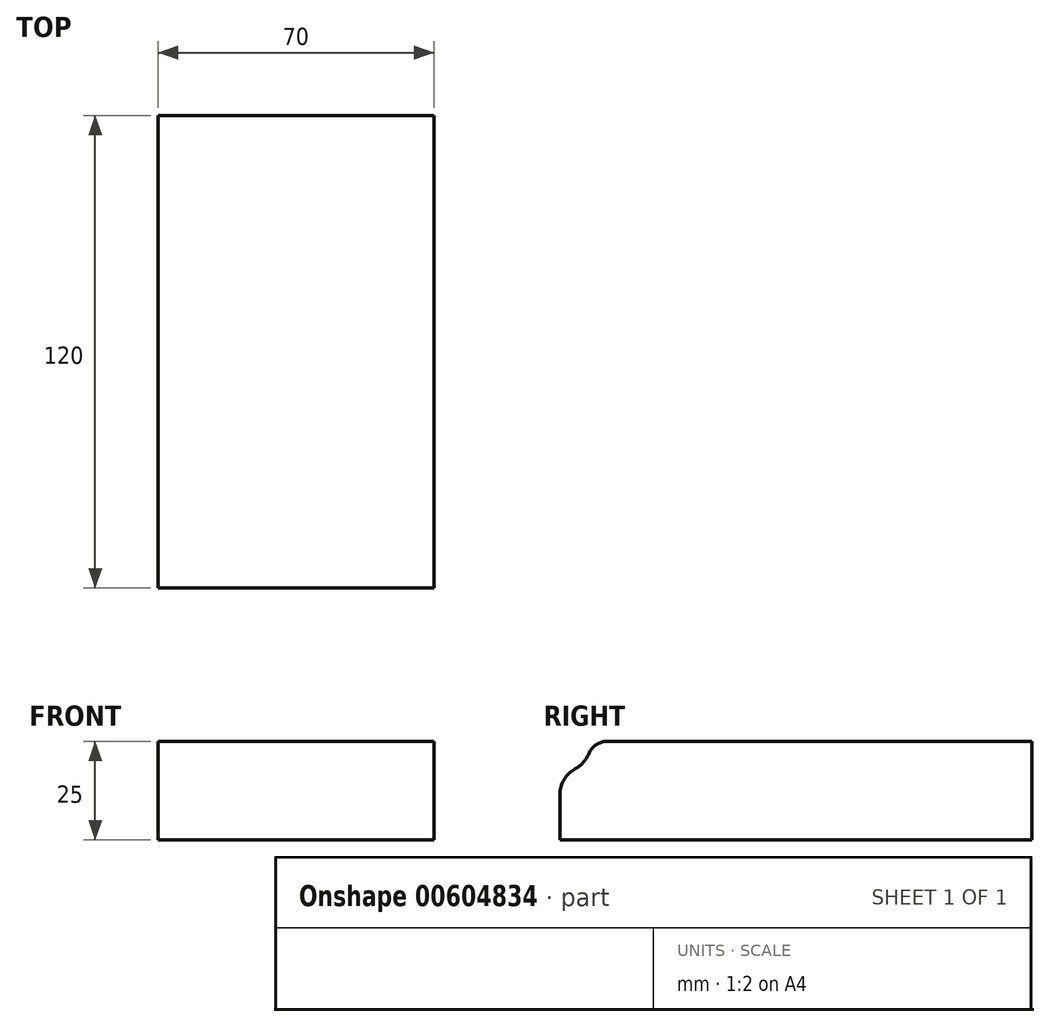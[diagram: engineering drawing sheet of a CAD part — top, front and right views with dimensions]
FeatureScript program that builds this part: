
annotation { "Feature Type Name" : "Feature", "Feature Type Description" : "" }
export const myFeature = defineFeature(function(context is Context, id is Id, definition is map)
    precondition{}
    {
        {
            var Q0;
            Q0=qCreatedBy(makeId("Top.planeOp"),FACE);
            var sketch = newSketch(context, id + "F0", { "sketchPlane" : qUnion([Q0])});
            skLineSegment(sketch, "E0.bottom", {"start": v(-35, -60) * mm, "end": v(35, -60) * mm});
            skLineSegment(sketch, "E0.top", {"start": v(-35, 60) * mm, "end": v(35, 60) * mm});
            skLineSegment(sketch, "E0.left", {"start": v(-35, -60) * mm, "end": v(-35, 60) * mm});
            skLineSegment(sketch, "E0.right", {"start": v(35, -60) * mm, "end": v(35, 60) * mm});
            skPoint(sketch, "E0.middle", {"position": v(0, 0) * mm});
            skSolve(sketch);
        }
        {
            var Q0;
            Q0=makeQuery(id+"F0.imprint","IMPRINT",FACE,{"disambiguationData":[TD([[makeQuery(id+"F0.imprint","IMPRINT",EDGE,{"derivedFrom":sQuery(id+"F0.wireOp",EDGE,"E0.bottom")}),1.0]])]});
            extrude(context, id + "F1", {"entities" : qUnion([Q0]), "depth" : 25 * mm, "offsetDistance" : 25 * mm});
        }
        {
            var Q0;
            Q0=makeQuery(id+"F1.opExtrude","SWEPT_FACE",FACE,{"disambiguationData":[OSD([sQuery(id+"F0.wireOp",EDGE,"E0.right")])]});
            var sketch = newSketch(context, id + "F2", { "sketchPlane" : qUnion([Q0])});
            skCircle(sketch, "E1", {"center": v(-60, 25) * mm, "radius": 8 * mm});
            skSolve(sketch);
        }
        {
            var Q0;
            Q0 = qSketchRegion(id + "F2", true);
            var Q1;
            Q1=makeQuery(id+"F1.opExtrude","SWEPT_FACE",FACE,{"disambiguationData":[OSD([sQuery(id+"F0.wireOp",EDGE,"E0.left")])]});
            extrude(context, id + "F3", {"entities" : qUnion([Q0]), "operationType" : NewBodyOperationType.REMOVE, "endBound" : BoundingType.UP_TO_SURFACE, "oppositeDirection" : true, "depth" : 25 * mm, "endBoundEntityFace" : qUnion([Q1]), "offsetDistance" : 25 * mm});
        }
        {
            var Q0;
            Q0=makeQuery(id+"F3.boolean.opBoolean","INTERSECT",EDGE,{"derivedFrom":[makeQuery(id+"F1.opExtrude","CAP_FACE",FACE,{"disambiguationData":[OSD([sQuery(id+"F0.wireOp",EDGE,"E0.bottom"),sQuery(id+"F0.wireOp",EDGE,"E0.top"),sQuery(id+"F0.wireOp",EDGE,"E0.left"),sQuery(id+"F0.wireOp",EDGE,"E0.right")])],"isStart":false}),makeQuery(id+"F3.opExtrude","SWEPT_FACE",FACE,{"disambiguationData":[OSD([sQuery(id+"F2.wireOp",EDGE,"E1")])]})]});
            fillet(context, id + "F4", {"entities" : qUnion([Q0]), "tangentPropagation" : true, "radius" : 5 * mm, "defaultsChanged" : false, "vertexSettings" : [], "allowEdgeOverflow" : false});
        }
        {
            var Q0;
            Q0=makeQuery(id+"F3.boolean.opBoolean","INTERSECT",EDGE,{"derivedFrom":[makeQuery(id+"F1.opExtrude","SWEPT_FACE",FACE,{"disambiguationData":[OSD([sQuery(id+"F0.wireOp",EDGE,"E0.bottom")])]}),makeQuery(id+"F3.opExtrude","SWEPT_FACE",FACE,{"disambiguationData":[OSD([sQuery(id+"F2.wireOp",EDGE,"E1")])]})]});
            fillet(context, id + "F5", {"entities" : qUnion([Q0]), "tangentPropagation" : true, "radius" : 7.5 * mm, "defaultsChanged" : true, "vertexSettings" : [], "allowEdgeOverflow" : false});
        }
    });
